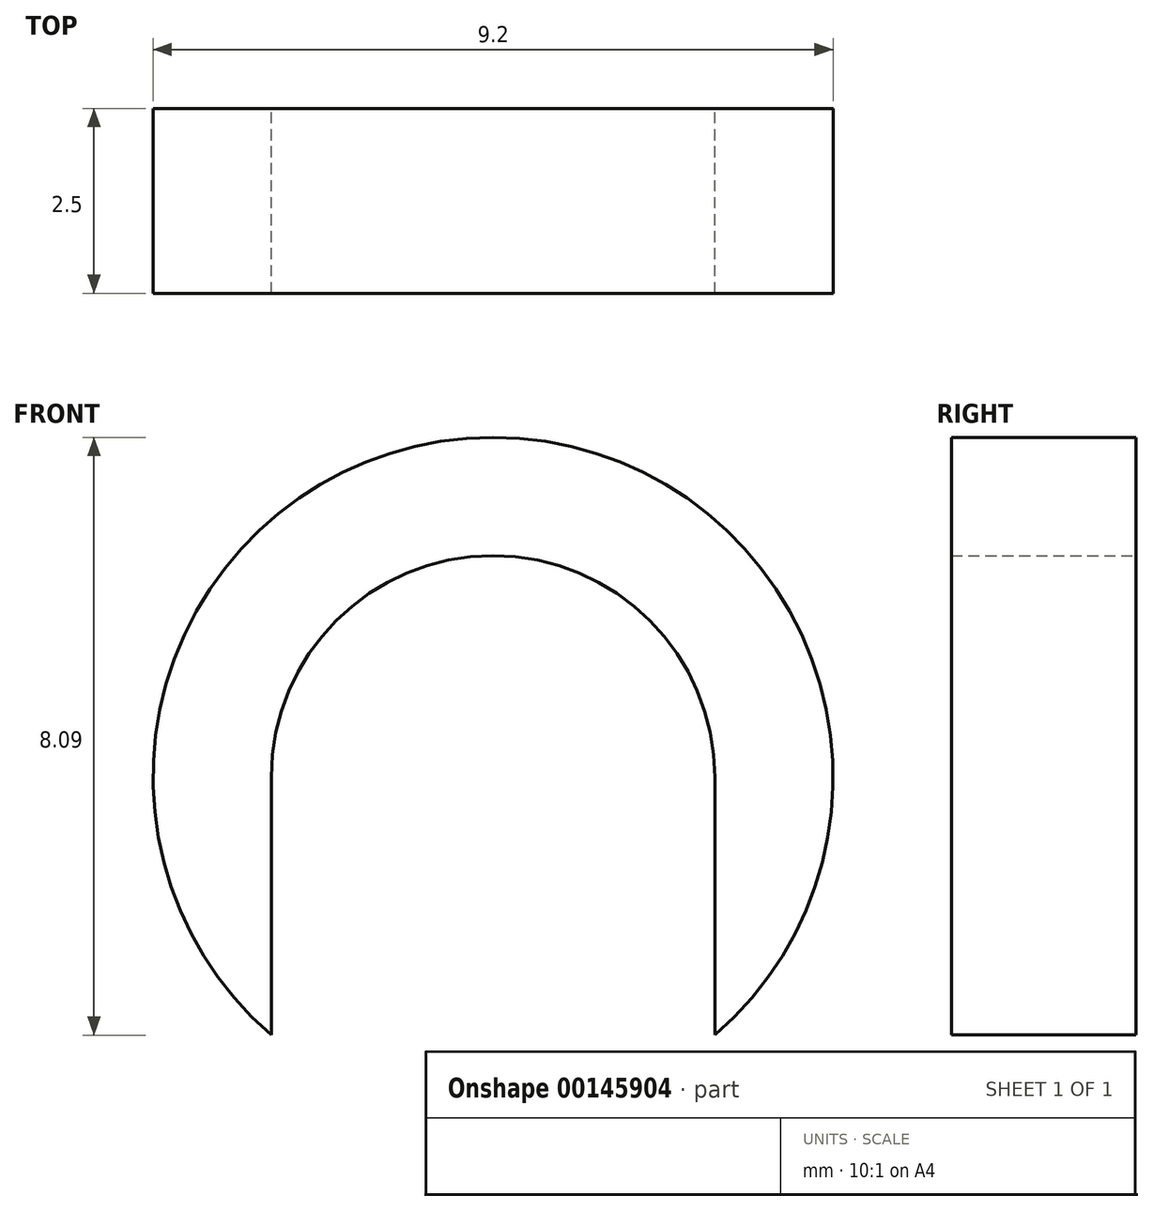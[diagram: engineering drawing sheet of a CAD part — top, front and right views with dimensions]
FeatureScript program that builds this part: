
annotation { "Feature Type Name" : "Feature", "Feature Type Description" : "" }
export const myFeature = defineFeature(function(context is Context, id is Id, definition is map)
    precondition{}
    {
        {
            var Q0;
            Q0=qCreatedBy(makeId("Front.planeOp"),FACE);
            var sketch = newSketch(context, id + "F0", { "sketchPlane" : qUnion([Q0])});
            skLineSegment(sketch, "E0.bottom", {"start": v(20, 66.9) * mm, "end": v(-20, 66.9) * mm});
            skLineSegment(sketch, "E0.top", {"start": v(20, -66.9) * mm, "end": v(-20, -66.9) * mm});
            skLineSegment(sketch, "E0.left", {"start": v(20, 66.9) * mm, "end": v(20, -66.9) * mm});
            skLineSegment(sketch, "E0.right", {"start": v(-20, 66.9) * mm, "end": v(-20, -66.9) * mm});
            skPoint(sketch, "E0.middle", {"position": v(0, 0) * mm});
            skLineSegment(sketch, "E1.bottom", {"start": v(20, -62.9) * mm, "end": v(76, -62.9) * mm});
            skLineSegment(sketch, "E1.top", {"start": v(20, 76.06) * mm, "end": v(76, 76.06) * mm});
            skLineSegment(sketch, "E1.left", {"start": v(20, -62.9) * mm, "end": v(20, 76.06) * mm});
            skLineSegment(sketch, "E1.right", {"start": v(76, -62.9) * mm, "end": v(76, 76.06) * mm});
            skLineSegment(sketch, "E2", {"start": v(0, 43.22) * mm, "end": v(0, -37.87) * mm, "construction": true});
            skCircle(sketch, "E3", {"center": v(68.75, 59.26) * mm, "radius": 3.5 * mm});
            skCircle(sketch, "E4", {"center": v(68.75, -33.17) * mm, "radius": 3.5 * mm});
            skCircle(sketch, "E5", {"center": v(50.75, 68.6) * mm, "radius": 2.5 * mm});
            skCircle(sketch, "E6", {"center": v(50.75, -55.4) * mm, "radius": 2.5 * mm});
            skLineSegment(sketch, "E7.MirrorCS", {"start": v(-20, 66.9) * mm, "end": v(20, 66.9) * mm});
            skLineSegment(sketch, "E8.MirrorCS", {"start": v(-20, -66.9) * mm, "end": v(20, -66.9) * mm});
            skCircle(sketch, "E9.MirrorC", {"center": v(-50.75, -55.4) * mm, "radius": 2.5 * mm});
            skCircle(sketch, "E10.MirrorC", {"center": v(-68.75, -33.17) * mm, "radius": 3.5 * mm});
            skLineSegment(sketch, "E11.MirrorCS", {"start": v(-20, -62.9) * mm, "end": v(-76, -62.9) * mm});
            skLineSegment(sketch, "E12.MirrorCS", {"start": v(-20, 76.06) * mm, "end": v(-76, 76.06) * mm});
            skCircle(sketch, "E13.MirrorC", {"center": v(-68.75, 59.26) * mm, "radius": 3.5 * mm});
            skCircle(sketch, "E14.MirrorC", {"center": v(-50.75, 68.6) * mm, "radius": 2.5 * mm});
            skLineSegment(sketch, "E15.MirrorCS", {"start": v(-76, -62.9) * mm, "end": v(-76, 76.06) * mm});
            skLineSegment(sketch, "E16.MirrorCS", {"start": v(-20, -62.9) * mm, "end": v(-20, 76.06) * mm});
            skLineSegment(sketch, "E17.bottom", {"start": v(150.22, -133.4) * mm, "end": v(-150.22, -133.4) * mm, "construction": true});
            skLineSegment(sketch, "E17.top", {"start": v(150.22, -153.43) * mm, "end": v(-150.22, -153.43) * mm, "construction": true});
            skLineSegment(sketch, "E17.left", {"start": v(150.22, -133.4) * mm, "end": v(150.22, -153.43) * mm, "construction": true});
            skLineSegment(sketch, "E17.right", {"start": v(-150.22, -133.4) * mm, "end": v(-150.22, -153.43) * mm, "construction": true});
            skPoint(sketch, "E17.middle", {"position": v(0, -143.42) * mm});
            skCircle(sketch, "E18", {"center": v(34.5, -28.92) * mm, "radius": 10 * mm, "construction": true});
            skCircle(sketch, "E19", {"center": v(34.5, 34.93) * mm, "radius": 10 * mm, "construction": true});
            skCircle(sketch, "E20.MirrorC", {"center": v(-34.5, 34.93) * mm, "radius": 10 * mm, "construction": true});
            skCircle(sketch, "E21.MirrorC", {"center": v(-34.5, -28.92) * mm, "radius": 10 * mm, "construction": true});
            skLineSegment(sketch, "E22", {"start": v(44.5, 64.55) * mm, "end": v(44.5, -50.82) * mm, "construction": true});
            skLineSegment(sketch, "E23.MirrorCS", {"start": v(-44.5, 64.55) * mm, "end": v(-44.5, -50.82) * mm, "construction": true});
            skSolve(sketch);
        }
        {
            var Q0;
            Q0=qCreatedBy(makeId("Front.planeOp"),FACE);
            var sketch = newSketch(context, id + "F1", { "sketchPlane" : qUnion([Q0])});
            skLineSegment(sketch, "E24", {"start": v(50.75, -55.4) * mm, "end": v(50.75, -9.9) * mm, "construction": true});
            skArc(sketch, "E25", {"start": v(53.75, -55.4) * mm, "mid": v(50.75, -58.4) * mm, "end": v(47.75, -55.4) * mm});
            skLineSegment(sketch, "E26", {"start": v(53.75, -55.4) * mm, "end": v(53.75, -30.41) * mm});
            skLineSegment(sketch, "E27", {"start": v(47.75, -55.4) * mm, "end": v(47.75, -32.65) * mm});
            skLineSegment(sketch, "E28", {"start": v(47.75, -32.65) * mm, "end": v(50.75, -32.65) * mm});
            skLineSegment(sketch, "E29.MirrorCS", {"start": v(47.75, -55.4) * mm, "end": v(47.75, -30.41) * mm});
            skLineSegment(sketch, "E30.MirrorCS", {"start": v(53.75, -55.4) * mm, "end": v(53.75, -32.65) * mm});
            skArc(sketch, "E31.MirrorCS", {"start": v(53.75, -9.9) * mm, "mid": v(50.75, -6.9) * mm, "end": v(47.75, -9.9) * mm});
            skLineSegment(sketch, "E32.MirrorCS", {"start": v(53.75, -9.9) * mm, "end": v(53.75, -34.89) * mm});
            skLineSegment(sketch, "E33.MirrorCS", {"start": v(47.75, -9.9) * mm, "end": v(47.75, -32.65) * mm});
            skLineSegment(sketch, "E34.MirrorCS", {"start": v(53.75, -9.9) * mm, "end": v(53.75, -32.65) * mm});
            skLineSegment(sketch, "E35.MirrorCS", {"start": v(47.75, -9.9) * mm, "end": v(47.75, -34.89) * mm});
            skLineSegment(sketch, "E36", {"start": v(50.75, 68.6) * mm, "end": v(50.75, 114.1) * mm, "construction": true});
            skArc(sketch, "E37", {"start": v(53.75, 68.6) * mm, "mid": v(50.75, 65.6) * mm, "end": v(47.75, 68.6) * mm});
            skLineSegment(sketch, "E38", {"start": v(53.75, 68.6) * mm, "end": v(53.75, 91.52) * mm});
            skLineSegment(sketch, "E39", {"start": v(50.75, 91.35) * mm, "end": v(53.75, 91.52) * mm});
            skLineSegment(sketch, "E40", {"start": v(47.75, 68.6) * mm, "end": v(47.75, 91.35) * mm});
            skLineSegment(sketch, "E41", {"start": v(47.75, 91.35) * mm, "end": v(50.75, 91.35) * mm});
            skLineSegment(sketch, "E42.MirrorCS", {"start": v(47.75, 68.6) * mm, "end": v(47.75, 91.52) * mm});
            skLineSegment(sketch, "E43.MirrorCS", {"start": v(53.75, 68.6) * mm, "end": v(53.75, 91.35) * mm});
            skArc(sketch, "E44.MirrorCS", {"start": v(47.75, 68.6) * mm, "mid": v(50.75, 65.6) * mm, "end": v(53.75, 68.6) * mm});
            skLineSegment(sketch, "E45.MirrorCS", {"start": v(50.75, 91.35) * mm, "end": v(53.75, 91.17) * mm});
            skArc(sketch, "E46.MirrorCS", {"start": v(53.75, 114.1) * mm, "mid": v(50.75, 117.1) * mm, "end": v(47.75, 114.1) * mm});
            skLineSegment(sketch, "E47.MirrorCS", {"start": v(53.75, 114.1) * mm, "end": v(53.75, 91.17) * mm});
            skLineSegment(sketch, "E48.MirrorCS", {"start": v(47.75, 114.1) * mm, "end": v(47.75, 91.35) * mm});
            skArc(sketch, "E49.MirrorCS", {"start": v(47.75, 114.1) * mm, "mid": v(50.75, 117.1) * mm, "end": v(53.75, 114.1) * mm});
            skLineSegment(sketch, "E50.MirrorCS", {"start": v(53.75, 114.1) * mm, "end": v(53.75, 91.35) * mm});
            skLineSegment(sketch, "E51.MirrorCS", {"start": v(47.75, 114.1) * mm, "end": v(47.75, 91.17) * mm});
            skLineSegment(sketch, "E52", {"start": v(63.25, -72.58) * mm, "end": v(63.25, 121.7) * mm});
            skLineSegment(sketch, "E53", {"start": v(63.25, 121.7) * mm, "end": v(39.4, 121.7) * mm});
            skLineSegment(sketch, "E54", {"start": v(23, 75.6) * mm, "end": v(23, -72.58) * mm});
            skLineSegment(sketch, "E55", {"start": v(23, -72.58) * mm, "end": v(0, -72.58) * mm});
            skCircle(sketch, "E56", {"center": v(50.75, -9.9) * mm, "radius": 4.6 * mm});
            skCircle(sketch, "E57", {"center": v(50.75, -55.4) * mm, "radius": 4.6 * mm});
            skCircle(sketch, "E58", {"center": v(50.75, 68.6) * mm, "radius": 4.6 * mm});
            skCircle(sketch, "E59", {"center": v(50.75, 114.1) * mm, "radius": 4.6 * mm});
            skLineSegment(sketch, "E60", {"start": v(23, 75.6) * mm, "end": v(39.4, 121.7) * mm});
            skLineSegment(sketch, "E61.bottom", {"start": v(26.16, -72.58) * mm, "end": v(34.1, -72.58) * mm});
            skLineSegment(sketch, "E61.top", {"start": v(26.16, -68.9) * mm, "end": v(34.1, -68.9) * mm});
            skLineSegment(sketch, "E61.left", {"start": v(26.16, -72.58) * mm, "end": v(26.16, -68.9) * mm});
            skLineSegment(sketch, "E61.right", {"start": v(34.1, -72.58) * mm, "end": v(34.1, -68.9) * mm});
            skLineSegment(sketch, "E62.1.0.0", {"start": v(47.1, -72.58) * mm, "end": v(47.1, -68.9) * mm});
            skLineSegment(sketch, "E62.1.0.1", {"start": v(39.16, -72.58) * mm, "end": v(39.16, -68.9) * mm});
            skLineSegment(sketch, "E62.1.0.2", {"start": v(39.16, -72.58) * mm, "end": v(47.1, -72.58) * mm});
            skLineSegment(sketch, "E62.1.0.3", {"start": v(39.16, -68.9) * mm, "end": v(47.1, -68.9) * mm});
            skLineSegment(sketch, "E62.2.0.0", {"start": v(60.1, -72.58) * mm, "end": v(60.1, -68.9) * mm});
            skLineSegment(sketch, "E62.2.0.1", {"start": v(52.16, -72.58) * mm, "end": v(52.16, -68.9) * mm});
            skLineSegment(sketch, "E62.2.0.2", {"start": v(52.16, -72.58) * mm, "end": v(60.1, -72.58) * mm});
            skLineSegment(sketch, "E62.2.0.3", {"start": v(52.16, -68.9) * mm, "end": v(60.1, -68.9) * mm});
            skLineSegment(sketch, "E62.direction1", {"start": v(26.16, -72.58) * mm, "end": v(39.16, -72.58) * mm, "construction": true});
            skLineSegment(sketch, "E63", {"start": v(26.16, -72.58) * mm, "end": v(23, -72.58) * mm, "construction": true});
            skLineSegment(sketch, "E64", {"start": v(60.1, -72.58) * mm, "end": v(63.25, -72.58) * mm, "construction": true});
            skArc(sketch, "E65.MirrorCS", {"start": v(-53.75, -9.9) * mm, "mid": v(-50.75, -6.9) * mm, "end": v(-47.75, -9.9) * mm});
            skLineSegment(sketch, "E66.MirrorCS", {"start": v(-50.75, 91.35) * mm, "end": v(-53.75, 91.17) * mm});
            skLineSegment(sketch, "E67.MirrorCS", {"start": v(-50.75, 91.35) * mm, "end": v(-53.75, 91.52) * mm});
            skLineSegment(sketch, "E68.MirrorCS", {"start": v(-47.75, 91.35) * mm, "end": v(-50.75, 91.35) * mm});
            skArc(sketch, "E69.MirrorCS", {"start": v(-47.75, 68.6) * mm, "mid": v(-50.75, 65.6) * mm, "end": v(-53.75, 68.6) * mm});
            skLineSegment(sketch, "E70.MirrorCS", {"start": v(-47.75, -32.65) * mm, "end": v(-50.75, -32.65) * mm});
            skLineSegment(sketch, "E71.MirrorCS", {"start": v(-26.16, -72.58) * mm, "end": v(-26.16, -68.9) * mm});
            skArc(sketch, "E72.MirrorCS", {"start": v(-53.75, 68.6) * mm, "mid": v(-50.75, 65.6) * mm, "end": v(-47.75, 68.6) * mm});
            skLineSegment(sketch, "E73.MirrorCS", {"start": v(-26.16, -72.58) * mm, "end": v(-23, -72.58) * mm, "construction": true});
            skArc(sketch, "E74.MirrorCS", {"start": v(-53.75, -55.4) * mm, "mid": v(-50.75, -58.4) * mm, "end": v(-47.75, -55.4) * mm});
            skLineSegment(sketch, "E75.MirrorCS", {"start": v(-60.1, -72.58) * mm, "end": v(-63.25, -72.58) * mm, "construction": true});
            skLineSegment(sketch, "E76.MirrorCS", {"start": v(-39.16, -72.58) * mm, "end": v(-39.16, -68.9) * mm});
            skLineSegment(sketch, "E77.MirrorCS", {"start": v(-60.1, -72.58) * mm, "end": v(-60.1, -68.9) * mm});
            skLineSegment(sketch, "E78.MirrorCS", {"start": v(-52.16, -68.9) * mm, "end": v(-60.1, -68.9) * mm});
            skLineSegment(sketch, "E79.MirrorCS", {"start": v(-52.16, -72.58) * mm, "end": v(-60.1, -72.58) * mm});
            skLineSegment(sketch, "E80.MirrorCS", {"start": v(-39.16, -68.9) * mm, "end": v(-47.1, -68.9) * mm});
            skLineSegment(sketch, "E81.MirrorCS", {"start": v(-26.16, -68.9) * mm, "end": v(-34.1, -68.9) * mm});
            skLineSegment(sketch, "E82.MirrorCS", {"start": v(-26.16, -72.58) * mm, "end": v(-39.16, -72.58) * mm, "construction": true});
            skLineSegment(sketch, "E83.MirrorCS", {"start": v(-52.16, -72.58) * mm, "end": v(-52.16, -68.9) * mm});
            skArc(sketch, "E84.MirrorCS", {"start": v(-47.75, 114.1) * mm, "mid": v(-50.75, 117.1) * mm, "end": v(-53.75, 114.1) * mm});
            skLineSegment(sketch, "E85.MirrorCS", {"start": v(-26.16, -72.58) * mm, "end": v(-34.1, -72.58) * mm});
            skLineSegment(sketch, "E86.MirrorCS", {"start": v(-47.1, -72.58) * mm, "end": v(-47.1, -68.9) * mm});
            skLineSegment(sketch, "E87.MirrorCS", {"start": v(-39.16, -72.58) * mm, "end": v(-47.1, -72.58) * mm});
            skLineSegment(sketch, "E88.MirrorCS", {"start": v(-34.1, -72.58) * mm, "end": v(-34.1, -68.9) * mm});
            skArc(sketch, "E89.MirrorCS", {"start": v(-53.75, 114.1) * mm, "mid": v(-50.75, 117.1) * mm, "end": v(-47.75, 114.1) * mm});
            skLineSegment(sketch, "E90.MirrorCS", {"start": v(-53.75, 114.1) * mm, "end": v(-53.75, 91.35) * mm});
            skLineSegment(sketch, "E91.MirrorCS", {"start": v(-47.75, 114.1) * mm, "end": v(-47.75, 91.35) * mm});
            skLineSegment(sketch, "E92.MirrorCS", {"start": v(-53.75, 68.6) * mm, "end": v(-53.75, 91.52) * mm});
            skLineSegment(sketch, "E93.MirrorCS", {"start": v(-47.75, 68.6) * mm, "end": v(-47.75, 91.52) * mm});
            skLineSegment(sketch, "E94.MirrorCS", {"start": v(-47.75, -9.9) * mm, "end": v(-47.75, -34.89) * mm});
            skLineSegment(sketch, "E95.MirrorCS", {"start": v(-53.75, -55.4) * mm, "end": v(-53.75, -30.41) * mm});
            skLineSegment(sketch, "E96.MirrorCS", {"start": v(-47.75, -55.4) * mm, "end": v(-47.75, -32.65) * mm});
            skLineSegment(sketch, "E97.MirrorCS", {"start": v(-53.75, -9.9) * mm, "end": v(-53.75, -32.65) * mm});
            skCircle(sketch, "E98.MirrorC", {"center": v(-50.75, -9.9) * mm, "radius": 4.6 * mm});
            skLineSegment(sketch, "E99.MirrorCS", {"start": v(-53.75, 114.1) * mm, "end": v(-53.75, 91.17) * mm});
            skLineSegment(sketch, "E100.MirrorCS", {"start": v(-23, -72.58) * mm, "end": v(0, -72.58) * mm});
            skLineSegment(sketch, "E101.MirrorCS", {"start": v(-53.75, 68.6) * mm, "end": v(-53.75, 91.35) * mm});
            skLineSegment(sketch, "E102.MirrorCS", {"start": v(-63.25, -72.58) * mm, "end": v(-63.25, 121.7) * mm});
            skCircle(sketch, "E103.MirrorC", {"center": v(-50.75, 114.1) * mm, "radius": 4.6 * mm});
            skCircle(sketch, "E104.MirrorC", {"center": v(-50.75, -55.4) * mm, "radius": 4.6 * mm});
            skLineSegment(sketch, "E105.MirrorCS", {"start": v(-63.25, 121.7) * mm, "end": v(-39.4, 121.7) * mm});
            skLineSegment(sketch, "E106.MirrorCS", {"start": v(-23, 75.6) * mm, "end": v(-39.4, 121.7) * mm});
            skLineSegment(sketch, "E107.MirrorCS", {"start": v(-53.75, -9.9) * mm, "end": v(-53.75, -34.89) * mm});
            skLineSegment(sketch, "E108.MirrorCS", {"start": v(-23, 75.6) * mm, "end": v(-23, -72.58) * mm});
            skLineSegment(sketch, "E109.MirrorCS", {"start": v(-50.75, 68.6) * mm, "end": v(-50.75, 114.1) * mm, "construction": true});
            skLineSegment(sketch, "E110.MirrorCS", {"start": v(-47.75, 114.1) * mm, "end": v(-47.75, 91.17) * mm});
            skLineSegment(sketch, "E111.MirrorCS", {"start": v(-47.75, -9.9) * mm, "end": v(-47.75, -32.65) * mm});
            skLineSegment(sketch, "E112.MirrorCS", {"start": v(-47.75, 68.6) * mm, "end": v(-47.75, 91.35) * mm});
            skLineSegment(sketch, "E113.MirrorCS", {"start": v(-50.75, -55.4) * mm, "end": v(-50.75, -9.9) * mm, "construction": true});
            skLineSegment(sketch, "E114.MirrorCS", {"start": v(-47.75, -55.4) * mm, "end": v(-47.75, -30.41) * mm});
            skCircle(sketch, "E115.MirrorC", {"center": v(-50.75, 68.6) * mm, "radius": 4.6 * mm});
            skLineSegment(sketch, "E116.MirrorCS", {"start": v(-53.75, -55.4) * mm, "end": v(-53.75, -32.65) * mm});
            skCircle(sketch, "E117", {"center": v(0, -163.58) * mm, "radius": 39 * mm});
            skCircle(sketch, "E118", {"center": v(76, -131.08) * mm, "radius": 16.5 * mm});
            skArc(sketch, "E119", {"start": v(-46, -163.58) * mm, "mid": v(-19.82, -205.09) * mm, "end": v(28.92, -199.35) * mm});
            skLineSegment(sketch, "E120", {"start": v(-46, -163.58) * mm, "end": v(-46, -106.75) * mm});
            skLineSegment(sketch, "E121", {"start": v(-46, -106.75) * mm, "end": v(-63.25, -72.58) * mm});
            skLineSegment(sketch, "E122", {"start": v(28.92, -199.35) * mm, "end": v(90.77, -149.35) * mm});
            skArc(sketch, "E123", {"start": v(90.77, -149.35) * mm, "mid": v(99.28, -134.27) * mm, "end": v(95.15, -117.46) * mm});
            skLineSegment(sketch, "E124", {"start": v(95.15, -117.46) * mm, "end": v(63.25, -72.58) * mm});
            skSolve(sketch);
        }
        {
            var Q0;
            {var subQ30=sQuery(id+"F1.wireOp",EDGE,"E32.MirrorCS");Q0=makeQuery(id+"F1.imprint","IMPRINT",FACE,{"disambiguationData":[TD([[makeQuery(id+"F1.imprint","IMPRINT",EDGE,{"derivedFrom":subQ30}),1.0]])]});}
            extrude(context, id + "F2", {"entities" : qUnion([Q0]), "depth" : 2.5 * mm});
        }
    });
